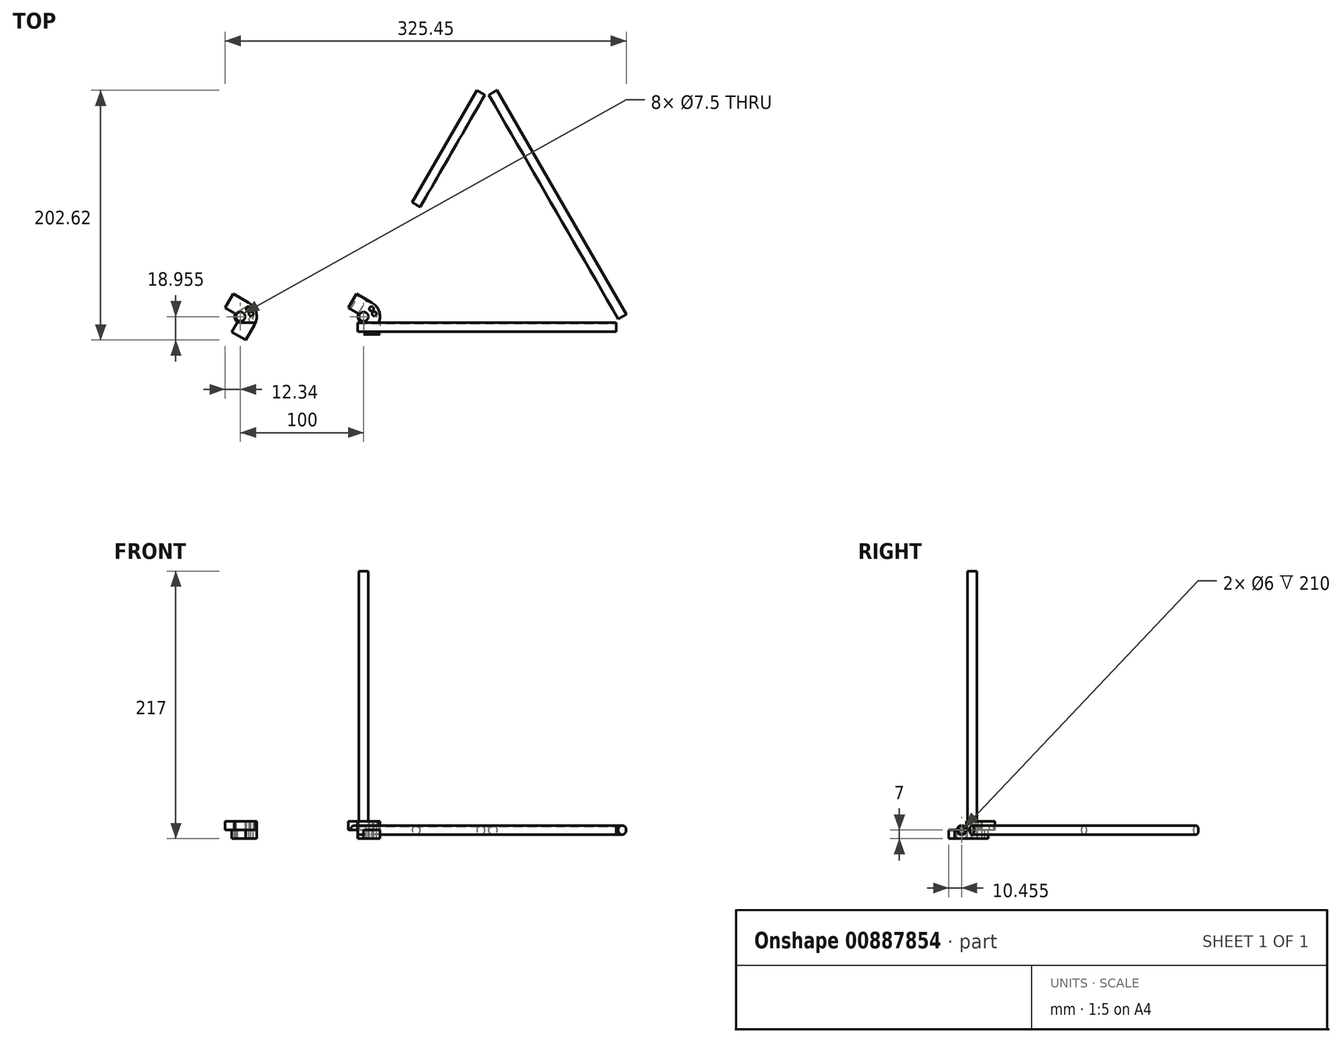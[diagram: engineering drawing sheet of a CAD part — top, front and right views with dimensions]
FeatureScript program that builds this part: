
annotation { "Feature Type Name" : "Feature", "Feature Type Description" : "" }
export const myFeature = defineFeature(function(context is Context, id is Id, definition is map)
    precondition{}
    {
        {
            var Q0;
            Q0=qCreatedBy(makeId("Top.planeOp"),FACE);
            var sketch = newSketch(context, id + "F0", { "sketchPlane" : qUnion([Q0])});
            skLineSegment(sketch, "E0", {"start": v(0, 115.47) * mm, "end": v(-100, -57.74) * mm});
            skLineSegment(sketch, "E1", {"start": v(-100, -57.74) * mm, "end": v(100, -57.74) * mm});
            skLineSegment(sketch, "E2", {"start": v(100, -57.74) * mm, "end": v(0, 115.47) * mm});
            skLineSegment(sketch, "E3", {"start": v(0, 0) * mm, "end": v(0, -57.74) * mm});
            skLineSegment(sketch, "E4", {"start": v(0, 0) * mm, "end": v(50, 28.87) * mm});
            skLineSegment(sketch, "E5", {"start": v(0, 0) * mm, "end": v(-50, 28.87) * mm});
            skLineSegment(sketch, "E6", {"start": v(0, 0) * mm, "end": v(-100, -57.74) * mm});
            skLineSegment(sketch, "E7", {"start": v(0, 0) * mm, "end": v(100, -57.74) * mm});
            skLineSegment(sketch, "E8", {"start": v(0, 0) * mm, "end": v(0, 115.47) * mm});
            skSolve(sketch);
        }
        {
            var Q0;
            Q0=sQuery(id+"F0.wireOp",EDGE,"E5");
            cPlane(context, id + "F1", {"entities" : qUnion([Q0]), "cplaneType" : CPlaneType.LINE_ANGLE, "offset" : 25 * mm, "angle" : 0 * degree, "width" : 150 * mm, "height" : 150 * mm});
        }
        {
            var Q0;
            Q0=sQuery(id+"F0.wireOp",EDGE,"E4");
            cPlane(context, id + "F2", {"entities" : qUnion([Q0]), "cplaneType" : CPlaneType.LINE_ANGLE, "offset" : 25 * mm, "angle" : 0 * degree, "width" : 150 * mm, "height" : 150 * mm});
        }
        {
            var Q0;
            Q0=sQuery(id+"F0.wireOp",EDGE,"E3");
            cPlane(context, id + "F3", {"entities" : qUnion([Q0]), "cplaneType" : CPlaneType.LINE_ANGLE, "offset" : 25 * mm, "angle" : 90 * degree, "oppositeDirection" : true, "width" : 150 * mm, "height" : 150 * mm});
        }
        {
            var Q0;
            Q0=qCreatedBy(makeId("Top.planeOp"),FACE);
            var sketch = newSketch(context, id + "F4", { "sketchPlane" : qUnion([Q0])});
            skLineSegment(sketch, "E9.bottom", {"start": v(-82.94, -28.18) * mm, "end": v(-29.24, -59.18) * mm});
            skLineSegment(sketch, "E9.top", {"start": v(-17.94, 84.4) * mm, "end": v(35.76, 53.4) * mm});
            skLineSegment(sketch, "E9.left", {"start": v(-82.94, -28.18) * mm, "end": v(-17.94, 84.4) * mm});
            skLineSegment(sketch, "E9.right", {"start": v(-29.24, -59.18) * mm, "end": v(35.76, 53.4) * mm});
            skLineSegment(sketch, "E10.0", {"start": v(0, 115.47) * mm, "end": v(-100, -57.74) * mm});
            skSolve(sketch);
        }
        {
            var Q0;
            Q0=qCreatedBy(makeId("Top.planeOp"),FACE);
            var sketch = newSketch(context, id + "F5", { "sketchPlane" : qUnion([Q0])});
            skPoint(sketch, "E11.0", {"position": v(-100, -57.74) * mm});
            skPoint(sketch, "E11.1", {"position": v(100, -57.74) * mm});
            skPoint(sketch, "E11.2", {"position": v(0, 115.47) * mm});
            skCircle(sketch, "E12", {"center": v(-100, -57.74) * mm, "radius": 3.75 * mm});
            skLineSegment(sketch, "E13", {"start": v(-106.61, -59.7) * mm, "end": v(-1.61, 122.18) * mm});
            skLineSegment(sketch, "E14", {"start": v(-113.1, -55.94) * mm, "end": v(-8.1, 125.93) * mm});
            skLineSegment(sketch, "E15", {"start": v(-1.61, 122.18) * mm, "end": v(-8.1, 125.93) * mm});
            skLineSegment(sketch, "E16", {"start": v(-106.61, -59.7) * mm, "end": v(-113.1, -55.94) * mm});
            skPoint(sketch, "E17", {"position": v(-54.11, 31.24) * mm});
            skCircle(sketch, "E18", {"center": v(0, 115.47) * mm, "radius": 3.75 * mm});
            skLineSegment(sketch, "E19", {"start": v(0, 115.47) * mm, "end": v(-3.25, 117.35) * mm});
            skLineSegment(sketch, "E20", {"start": v(-100, -57.74) * mm, "end": v(-103.25, -55.86) * mm});
            skCircle(sketch, "E21", {"center": v(100, -57.74) * mm, "radius": 3.75 * mm});
            skLineSegment(sketch, "E22.MirrorCS", {"start": v(106.61, -59.7) * mm, "end": v(1.61, 122.18) * mm});
            skLineSegment(sketch, "E23.MirrorCS", {"start": v(106.61, -59.7) * mm, "end": v(113.1, -55.94) * mm});
            skLineSegment(sketch, "E24.MirrorCS", {"start": v(113.1, -55.94) * mm, "end": v(8.1, 125.93) * mm});
            skLineSegment(sketch, "E25.MirrorCS", {"start": v(1.61, 122.18) * mm, "end": v(8.1, 125.93) * mm});
            skLineSegment(sketch, "E26.MirrorCS", {"start": v(-105, -62.49) * mm, "end": v(105, -62.49) * mm});
            skLineSegment(sketch, "E27.MirrorCS", {"start": v(-105, -62.49) * mm, "end": v(-105, -69.99) * mm});
            skLineSegment(sketch, "E28.MirrorCS", {"start": v(-105, -69.99) * mm, "end": v(105, -69.99) * mm});
            skLineSegment(sketch, "E29.MirrorCS", {"start": v(105, -62.49) * mm, "end": v(105, -69.99) * mm});
            skSolve(sketch);
        }
        {
            var Q0;
            Q0=qCreatedBy(makeId("Top.planeOp"),FACE);
            var sketch = newSketch(context, id + "F6", { "sketchPlane" : qUnion([Q0])});
            skPoint(sketch, "E30.0", {"position": v(-100, -57.74) * mm});
            skPoint(sketch, "E31.0", {"position": v(0, 115.47) * mm});
            skPoint(sketch, "E32.0", {"position": v(100, -57.74) * mm});
            skPoint(sketch, "E33.0", {"position": v(-113.1, -55.94) * mm});
            skCircle(sketch, "E34", {"center": v(-100, -57.74) * mm, "radius": 13.23 * mm});
            skCircle(sketch, "E35.MirrorC", {"center": v(100, -57.74) * mm, "radius": 13.23 * mm});
            skCircle(sketch, "E36.MirrorC", {"center": v(0, 115.47) * mm, "radius": 13.23 * mm});
            skSolve(sketch);
        }
        {
            var Q0;
            Q0=qCreatedBy(id+"F1.planeOp",FACE);
            var sketch = newSketch(context, id + "F7", { "sketchPlane" : qUnion([Q0])});
            skPoint(sketch, "E37.0", {"position": v(-66.24, 0) * mm});
            skCircle(sketch, "E38", {"center": v(-66.24, 0) * mm, "radius": 3.75 * mm});
            skPoint(sketch, "E39.0", {"position": v(-69.99, 0) * mm});
            skSolve(sketch);
        }
        {
            var Q0;
            Q0=qCreatedBy(id+"F2.planeOp",FACE);
            var sketch = newSketch(context, id + "F8", { "sketchPlane" : qUnion([Q0])});
            skPoint(sketch, "E40.0", {"position": v(-66.24, 0) * mm});
            skPoint(sketch, "E41.0", {"position": v(-69.99, 0) * mm});
            skCircle(sketch, "E42", {"center": v(-66.24, 0) * mm, "radius": 3.75 * mm});
            skSolve(sketch);
        }
        {
            var Q0;
            Q0=qCreatedBy(id+"F3.planeOp",FACE);
            var sketch = newSketch(context, id + "F9", { "sketchPlane" : qUnion([Q0])});
            skPoint(sketch, "E43.0", {"position": v(66.24, 0) * mm});
            skPoint(sketch, "E44.0", {"position": v(69.99, 0) * mm});
            skCircle(sketch, "E45", {"center": v(66.24, 0) * mm, "radius": 3.75 * mm});
            skSolve(sketch);
        }
        {
            var Q0;
            Q0=makeQuery(id+"F7.imprint","IMPRINT",FACE,{"disambiguationData":[TD([[makeQuery(id+"F7.imprint","IMPRINT",EDGE,{"derivedFrom":sQuery(id+"F7.wireOp",EDGE,"E38")}),1.0]])]});
            var Q1;
            Q1=sQuery(id+"F5.wireOp",EDGE,"E14");
            sweep(context, id + "F10", {"profiles" : qUnion([Q0]), "path" : qUnion([Q1])});
        }
        {
            var Q0;
            Q0=makeQuery(id+"F8.imprint","IMPRINT",FACE,{"disambiguationData":[TD([[makeQuery(id+"F8.imprint","IMPRINT",EDGE,{"derivedFrom":sQuery(id+"F8.wireOp",EDGE,"E42")}),1.0]])]});
            var Q1;
            Q1=sQuery(id+"F5.wireOp",EDGE,"E24.MirrorCS");
            sweep(context, id + "F11", {"profiles" : qUnion([Q0]), "path" : qUnion([Q1])});
        }
        {
            var Q0;
            Q0=makeQuery(id+"F9.imprint","IMPRINT",FACE,{"disambiguationData":[TD([[makeQuery(id+"F9.imprint","IMPRINT",EDGE,{"derivedFrom":sQuery(id+"F9.wireOp",EDGE,"E45")}),1.0]])]});
            var Q1;
            Q1=sQuery(id+"F5.wireOp",EDGE,"E28.MirrorCS");
            sweep(context, id + "F12", {"profiles" : qUnion([Q0]), "path" : qUnion([Q1])});
        }
        {
            var Q0;
            Q0=makeQuery(id+"F10.opSweep","CAP_FACE",FACE,{"disambiguationData":[OSD([sQuery(id+"F5.wireOp",VERTEX,"E14.start"),sQuery(id+"F7.wireOp",EDGE,"E38")])],"isStart":false});
            var sketch = newSketch(context, id + "F13", { "sketchPlane" : qUnion([Q0])});
            skPoint(sketch, "E46.0", {"position": v(-66.24, 0) * mm});
            skSolve(sketch);
        }
        {
            var Q0;
            Q0=makeQuery(id+"F11.opSweep","CAP_FACE",FACE,{"disambiguationData":[OSD([sQuery(id+"F5.wireOp",VERTEX,"E24.MirrorCS.start"),sQuery(id+"F8.wireOp",EDGE,"E42")])],"isStart":true});
            var sketch = newSketch(context, id + "F14", { "sketchPlane" : qUnion([Q0])});
            skPoint(sketch, "E47.0", {"position": v(66.24, 0) * mm});
            skSolve(sketch);
        }
        {
            var Q0;
            Q0=makeQuery(id+"F12.opSweep","CAP_FACE",FACE,{"disambiguationData":[OSD([sQuery(id+"F5.wireOp",VERTEX,"E28.MirrorCS.start"),sQuery(id+"F9.wireOp",EDGE,"E45")])],"isStart":false});
            var sketch = newSketch(context, id + "F15", { "sketchPlane" : qUnion([Q0])});
            skPoint(sketch, "E48.0", {"position": v(66.24, 0) * mm});
            skSolve(sketch);
        }
        {
            var Q0;
            Q0=sQuery(id+"F13.wireOp",VERTEX,"E46.0");
            var Q1;
            Q1=sQuery(id+"F14.wireOp",VERTEX,"E47.0");
            var Q2;
            Q2=sQuery(id+"F15.wireOp",VERTEX,"E48.0");
            var Q3;
            Q3=makeQuery(id+"F10.opSweep","SWEPT_BODY",BODY,{"disambiguationData":[OSD([sQuery(id+"F5.wireOp",EDGE,"E14"),sQuery(id+"F7.wireOp",EDGE,"E38")])]});
            var Q4;
            Q4=makeQuery(id+"F11.opSweep","SWEPT_BODY",BODY,{"disambiguationData":[OSD([sQuery(id+"F5.wireOp",EDGE,"E24.MirrorCS"),sQuery(id+"F8.wireOp",EDGE,"E42")])]});
            var Q5;
            Q5=makeQuery(id+"F12.opSweep","SWEPT_BODY",BODY,{"disambiguationData":[OSD([sQuery(id+"F5.wireOp",EDGE,"E28.MirrorCS"),sQuery(id+"F9.wireOp",EDGE,"E45")])]});
            hole(context, id + "F16", {"style" : HoleStyle.SIMPLE, "endStyle" : HoleEndStyle.THROUGH, "standardTappedOrClearance" : lookupTablePath({ "standard" : "ISO", "size" : "6", "type" : "Drilled" }), "standardBlindInLast" : lookupTablePath({ "standard" : "ISO", "size" : "6", "type" : "Drilled" }), "holeDiameter" : 6 * mm, "majorDiameter" : 5 * mm, "isTappedThrough" : true, "tappedDepth" : 6 * mm, "tapClearance" : 3, "locations" : qUnion([Q0, Q1, Q2]), "scope" : qUnion([Q3, Q4, Q5])});
        }
        {
            var Q0;
            Q0=qCreatedBy(id+"F1.planeOp",FACE);
            var sketch = newSketch(context, id + "F17", { "sketchPlane" : qUnion([Q0])});
            skPoint(sketch, "E49.0", {"position": v(-57.74, 0) * mm});
            skLineSegment(sketch, "E50", {"start": v(-57.74, 0) * mm, "end": v(-57.74, 210) * mm});
            skSolve(sketch);
        }
        {
            var Q0;
            Q0=makeQuery(id+"F5.imprint","IMPRINT",FACE,{"disambiguationData":[TD([[makeQuery(id+"F5.imprint","IMPRINT",EDGE,{"derivedFrom":sQuery(id+"F5.wireOp",EDGE,"E12")}),1.0]])]});
            var Q1;
            Q1=sQuery(id+"F17.wireOp",EDGE,"E50");
            sweep(context, id + "F18", {"profiles" : qUnion([Q0]), "path" : qUnion([Q1])});
        }
        {
            var Q0;
            Q0=qCreatedBy(makeId("Top.planeOp"),FACE);
            var sketch = newSketch(context, id + "F19", { "sketchPlane" : qUnion([Q0])});
            skPoint(sketch, "E51", {"position": v(-93.38, -46.28) * mm});
            skLineSegment(sketch, "E52", {"start": v(-93.38, -46.28) * mm, "end": v(-105.73, -39.15) * mm});
            skLineSegment(sketch, "E53", {"start": v(-105.73, -39.15) * mm, "end": v(-112.34, -50.61) * mm});
            skPoint(sketch, "E54.0", {"position": v(-103.25, -55.86) * mm});
            skLineSegment(sketch, "E55", {"start": v(-103.25, -55.86) * mm, "end": v(-112.34, -50.61) * mm});
            skPoint(sketch, "E56.0", {"position": v(-100, -57.74) * mm});
            skPoint(sketch, "E57.MirrorP", {"position": v(-100, -61.49) * mm});
            skLineSegment(sketch, "E58", {"start": v(-100, -61.49) * mm, "end": v(-100, -62.49) * mm});
            skCircle(sketch, "E59", {"center": v(-100, -57.74) * mm, "radius": 3.75 * mm});
            skCircle(sketch, "E60", {"center": v(-100, -57.74) * mm, "radius": 4.75 * mm});
            skPoint(sketch, "E61", {"position": v(-104.11, -55.36) * mm});
            skLineSegment(sketch, "E62", {"start": v(-100, -62.49) * mm, "end": v(-87.65, -62.49) * mm});
            skArc(sketch, "E63", {"start": v(-87.65, -62.49) * mm, "mid": v(-87.53, -53.32) * mm, "end": v(-93.38, -46.28) * mm});
            skArc(sketch, "E64", {"start": v(-103.25, -55.86) * mm, "mid": v(-103.25, -59.61) * mm, "end": v(-100, -61.49) * mm});
            skPoint(sketch, "E65", {"position": v(-97.94, -44.67) * mm});
            skPoint(sketch, "E66", {"position": v(-97.5, -43.9) * mm});
            skPoint(sketch, "E67", {"position": v(-86.77, -57.74) * mm});
            skLineSegment(sketch, "E68", {"start": v(-100, -57.74) * mm, "end": v(-93.38, -46.28) * mm});
            skLineSegment(sketch, "E69", {"start": v(-100, -57.74) * mm, "end": v(-86.77, -57.74) * mm});
            skLineSegment(sketch, "E70", {"start": v(-100, -57.74) * mm, "end": v(-90.64, -48.38) * mm});
            skLineSegment(sketch, "E71", {"start": v(-100, -57.74) * mm, "end": v(-87.22, -54.31) * mm});
            skPoint(sketch, "E72", {"position": v(-96.64, -54.38) * mm});
            skPoint(sketch, "E73", {"position": v(-95.41, -56.5) * mm});
            skPoint(sketch, "E74", {"position": v(-93.64, -51.38) * mm});
            skPoint(sketch, "E75", {"position": v(-91.32, -55.4) * mm});
            skCircle(sketch, "E76", {"center": v(-91.32, -55.4) * mm, "radius": 1.8 * mm});
            skCircle(sketch, "E77", {"center": v(-93.64, -51.38) * mm, "radius": 1.8 * mm});
            skSolve(sketch);
        }
        {
            var Q0;
            Q0=makeQuery(id+"F19.imprint","IMPRINT",FACE,{"disambiguationData":[TD([[makeQuery(id+"F19.imprint","IMPRINT",EDGE,{"derivedFrom":sQuery(id+"F19.wireOp",EDGE,"E52")}),1.0]])]});
            var Q1;
            {var subQ5=sQuery(id+"F19.wireOp",EDGE,"E58");Q1=makeQuery(id+"F19.imprint","IMPRINT",FACE,{"disambiguationData":[TD([[makeQuery(id+"F19.imprint","IMPRINT",EDGE,{"derivedFrom":subQ5}),1.0]])]});}
            var Q2;
            {var subQ5=sQuery(id+"F19.wireOp",EDGE,"E58");Q2=makeQuery(id+"F19.imprint","IMPRINT",FACE,{"disambiguationData":[TD([[makeQuery(id+"F19.imprint","IMPRINT",EDGE,{"derivedFrom":subQ5}),-1.0]])]});}
            var Q3;
            {var subQ0=sQuery(id+"F19.wireOp",EDGE,"E59");var subQ1=sQuery(id+"F19.wireOp",EDGE,"E55");var subQ2=makeQuery(id+"F19.imprint","INTERSECT",VERTEX,{"derivedFrom":[subQ1,subQ0]});Q3=makeQuery(id+"F19.imprint","IMPRINT",FACE,{"disambiguationData":[TD([[makeQuery(id+"F19.imprint","IMPRINT",EDGE,{"disambiguationData":[TD([[subQ2,-1.0]])],"derivedFrom":subQ1}),-1.0]])]});}
            var Q4;
            {var subQ0=sQuery(id+"F19.wireOp",EDGE,"E70");var subQ1=sQuery(id+"F19.wireOp",EDGE,"E60");var subQ2=makeQuery(id+"F19.imprint","INTERSECT",VERTEX,{"derivedFrom":[subQ1,subQ0]});Q4=makeQuery(id+"F19.imprint","IMPRINT",FACE,{"disambiguationData":[TD([[makeQuery(id+"F19.imprint","IMPRINT",EDGE,{"disambiguationData":[TD([[subQ2,-1.0]])],"derivedFrom":subQ1}),-1.0]])]});}
            var Q5;
            {var subQ0=sQuery(id+"F19.wireOp",EDGE,"E71");var subQ1=sQuery(id+"F19.wireOp",EDGE,"E60");var subQ2=makeQuery(id+"F19.imprint","INTERSECT",VERTEX,{"derivedFrom":[subQ1,subQ0]});Q5=makeQuery(id+"F19.imprint","IMPRINT",FACE,{"disambiguationData":[TD([[makeQuery(id+"F19.imprint","IMPRINT",EDGE,{"disambiguationData":[TD([[subQ2,-1.0]])],"derivedFrom":subQ1}),-1.0]])]});}
            var Q6;
            {var subQ0=sQuery(id+"F19.wireOp",EDGE,"E71");var subQ1=sQuery(id+"F19.wireOp",EDGE,"E60");var subQ2=makeQuery(id+"F19.imprint","INTERSECT",VERTEX,{"derivedFrom":[subQ1,subQ0]});Q6=makeQuery(id+"F19.imprint","IMPRINT",FACE,{"disambiguationData":[TD([[makeQuery(id+"F19.imprint","IMPRINT",EDGE,{"disambiguationData":[TD([[subQ2,1.0]])],"derivedFrom":subQ1}),-1.0]])]});}
            var Q7;
            {var subQ0=sQuery(id+"F19.wireOp",EDGE,"E62");Q7=makeQuery(id+"F19.imprint","IMPRINT",FACE,{"disambiguationData":[TD([[makeQuery(id+"F19.imprint","IMPRINT",EDGE,{"derivedFrom":subQ0}),1.0]])]});}
            var Q8;
            {var subQ0=sQuery(id+"F19.wireOp",EDGE,"E70");var subQ1=sQuery(id+"F19.wireOp",EDGE,"E59");var subQ2=makeQuery(id+"F19.imprint","INTERSECT",VERTEX,{"derivedFrom":[subQ1,subQ0]});Q8=makeQuery(id+"F19.imprint","IMPRINT",FACE,{"disambiguationData":[TD([[makeQuery(id+"F19.imprint","IMPRINT",EDGE,{"disambiguationData":[TD([[subQ2,-1.0]])],"derivedFrom":subQ1}),-1.0]])]});}
            var Q9;
            {var subQ0=sQuery(id+"F19.wireOp",EDGE,"E71");var subQ1=sQuery(id+"F19.wireOp",EDGE,"E59");var subQ2=makeQuery(id+"F19.imprint","INTERSECT",VERTEX,{"derivedFrom":[subQ1,subQ0]});Q9=makeQuery(id+"F19.imprint","IMPRINT",FACE,{"disambiguationData":[TD([[makeQuery(id+"F19.imprint","IMPRINT",EDGE,{"disambiguationData":[TD([[subQ2,-1.0]])],"derivedFrom":subQ1}),-1.0]])]});}
            var Q10;
            {var subQ0=sQuery(id+"F19.wireOp",EDGE,"E71");var subQ1=sQuery(id+"F19.wireOp",EDGE,"E59");var subQ2=makeQuery(id+"F19.imprint","INTERSECT",VERTEX,{"derivedFrom":[subQ1,subQ0]});Q10=makeQuery(id+"F19.imprint","IMPRINT",FACE,{"disambiguationData":[TD([[makeQuery(id+"F19.imprint","IMPRINT",EDGE,{"disambiguationData":[TD([[subQ2,1.0]])],"derivedFrom":subQ1}),-1.0]])]});}
            extrude(context, id + "F20", {"entities" : qUnion([Q0, Q1, Q2, Q3, Q4, Q5, Q6, Q7, Q8, Q9, Q10]), "depth" : 7 * mm, "offsetDistance" : 25 * mm});
        }
        {
            var Q0;
            Q0=makeQuery(id+"F20.opExtrude","SWEPT_BODY",BODY,{"disambiguationData":[OSD([sQuery(id+"F19.wireOp",EDGE,"E52"),sQuery(id+"F19.wireOp",EDGE,"E53"),sQuery(id+"F19.wireOp",EDGE,"E55"),sQuery(id+"F19.wireOp",EDGE,"E58"),sQuery(id+"F19.wireOp",EDGE,"E59"),sQuery(id+"F19.wireOp",EDGE,"E62"),sQuery(id+"F19.wireOp",EDGE,"E63")])]});
            var Q1;
            Q1=sQuery(id+"F0.wireOp",EDGE,"E0");
            var Q2;
            Q2=sQuery(id+"F0.wireOp",EDGE,"E0");
            transform(context, id + "F21", {"entities" : qUnion([Q0]), "transformType" : TransformType.ROTATION, "transformAxis" : qUnion([Q2]), "angle" : 180 * degree, "makeCopy" : true});
        }
        {
            var Q0;
            Q0=makeQuery(id+"F21.opPattern","COPY",BODY,{"derivedFrom":makeQuery(id+"F20.opExtrude","SWEPT_BODY",BODY,{"disambiguationData":[OSD([sQuery(id+"F19.wireOp",EDGE,"E52"),sQuery(id+"F19.wireOp",EDGE,"E53"),sQuery(id+"F19.wireOp",EDGE,"E55"),sQuery(id+"F19.wireOp",EDGE,"E58"),sQuery(id+"F19.wireOp",EDGE,"E59"),sQuery(id+"F19.wireOp",EDGE,"E62"),sQuery(id+"F19.wireOp",EDGE,"E63")])]}),"instanceName":"1"});
            var Q1;
            Q1=makeQuery(id+"F18.opSweep","SWEPT_FACE",FACE,{"disambiguationData":[OSD([sQuery(id+"F5.wireOp",EDGE,"E12"),sQuery(id+"F17.wireOp",EDGE,"E50")])]});
            transform(context, id + "F22", {"entities" : qUnion([Q0]), "transformType" : TransformType.ROTATION, "transformAxis" : qUnion([Q1]), "angle" : 60 * degree, "oppositeDirection" : true, "makeCopy" : false});
        }
        {
            var Q0;
            Q0=makeQuery(id+"F20.opExtrude","SWEPT_BODY",BODY,{"disambiguationData":[OSD([sQuery(id+"F19.wireOp",EDGE,"E52"),sQuery(id+"F19.wireOp",EDGE,"E53"),sQuery(id+"F19.wireOp",EDGE,"E55"),sQuery(id+"F19.wireOp",EDGE,"E58"),sQuery(id+"F19.wireOp",EDGE,"E59"),sQuery(id+"F19.wireOp",EDGE,"E62"),sQuery(id+"F19.wireOp",EDGE,"E63")])]});
            transform(context, id + "F23", {"entities" : qUnion([Q0]), "transformType" : TransformType.TRANSLATION_3D, "dx" : -100 * mm, "dy" : 0 * mm, "dz" : 0 * mm, "makeCopy" : true});
        }
        {
            var Q0;
            Q0=makeQuery(id+"F21.opPattern","COPY",BODY,{"derivedFrom":makeQuery(id+"F20.opExtrude","SWEPT_BODY",BODY,{"disambiguationData":[OSD([sQuery(id+"F19.wireOp",EDGE,"E52"),sQuery(id+"F19.wireOp",EDGE,"E53"),sQuery(id+"F19.wireOp",EDGE,"E55"),sQuery(id+"F19.wireOp",EDGE,"E58"),sQuery(id+"F19.wireOp",EDGE,"E59"),sQuery(id+"F19.wireOp",EDGE,"E62"),sQuery(id+"F19.wireOp",EDGE,"E63")])]}),"instanceName":"1"});
            transform(context, id + "F24", {"entities" : qUnion([Q0]), "transformType" : TransformType.TRANSLATION_3D, "dx" : -100 * mm, "dy" : 0 * mm, "dz" : 0 * mm, "makeCopy" : true});
        }
        {
            var Q0;
            Q0=makeQuery(id+"F24.opPattern","COPY",BODY,{"derivedFrom":makeQuery(id+"F21.opPattern","COPY",BODY,{"derivedFrom":makeQuery(id+"F20.opExtrude","SWEPT_BODY",BODY,{"disambiguationData":[OSD([sQuery(id+"F19.wireOp",EDGE,"E52"),sQuery(id+"F19.wireOp",EDGE,"E53"),sQuery(id+"F19.wireOp",EDGE,"E55"),sQuery(id+"F19.wireOp",EDGE,"E58"),sQuery(id+"F19.wireOp",EDGE,"E59"),sQuery(id+"F19.wireOp",EDGE,"E62"),sQuery(id+"F19.wireOp",EDGE,"E63")])]}),"instanceName":"1"}),"instanceName":"1"});
            var Q1;
            Q1=makeQuery(id+"F23.opPattern","COPY",EDGE,{"derivedFrom":makeQuery(id+"F20.opExtrude","CAP_EDGE",EDGE,{"disambiguationData":[OSD([sQuery(id+"F19.wireOp",EDGE,"E59")])],"isStart":true}),"instanceName":"1"});
            transform(context, id + "F25", {"entities" : qUnion([Q0]), "transformType" : TransformType.ROTATION, "transformAxis" : qUnion([Q1]), "angle" : 30 * degree, "oppositeDirection" : true, "makeCopy" : false});
        }
        {
            var Q0;
            Q0=makeQuery(id+"F7.imprint","IMPRINT",FACE,{"disambiguationData":[TD([[makeQuery(id+"F7.imprint","IMPRINT",EDGE,{"derivedFrom":sQuery(id+"F7.wireOp",EDGE,"E38")}),1.0]])]});
            extrude(context, id + "F26", {"entities" : qUnion([Q0]), "operationType" : NewBodyOperationType.REMOVE, "depth" : 144.3 * mm, "offsetDistance" : 25 * mm});
        }
    });
